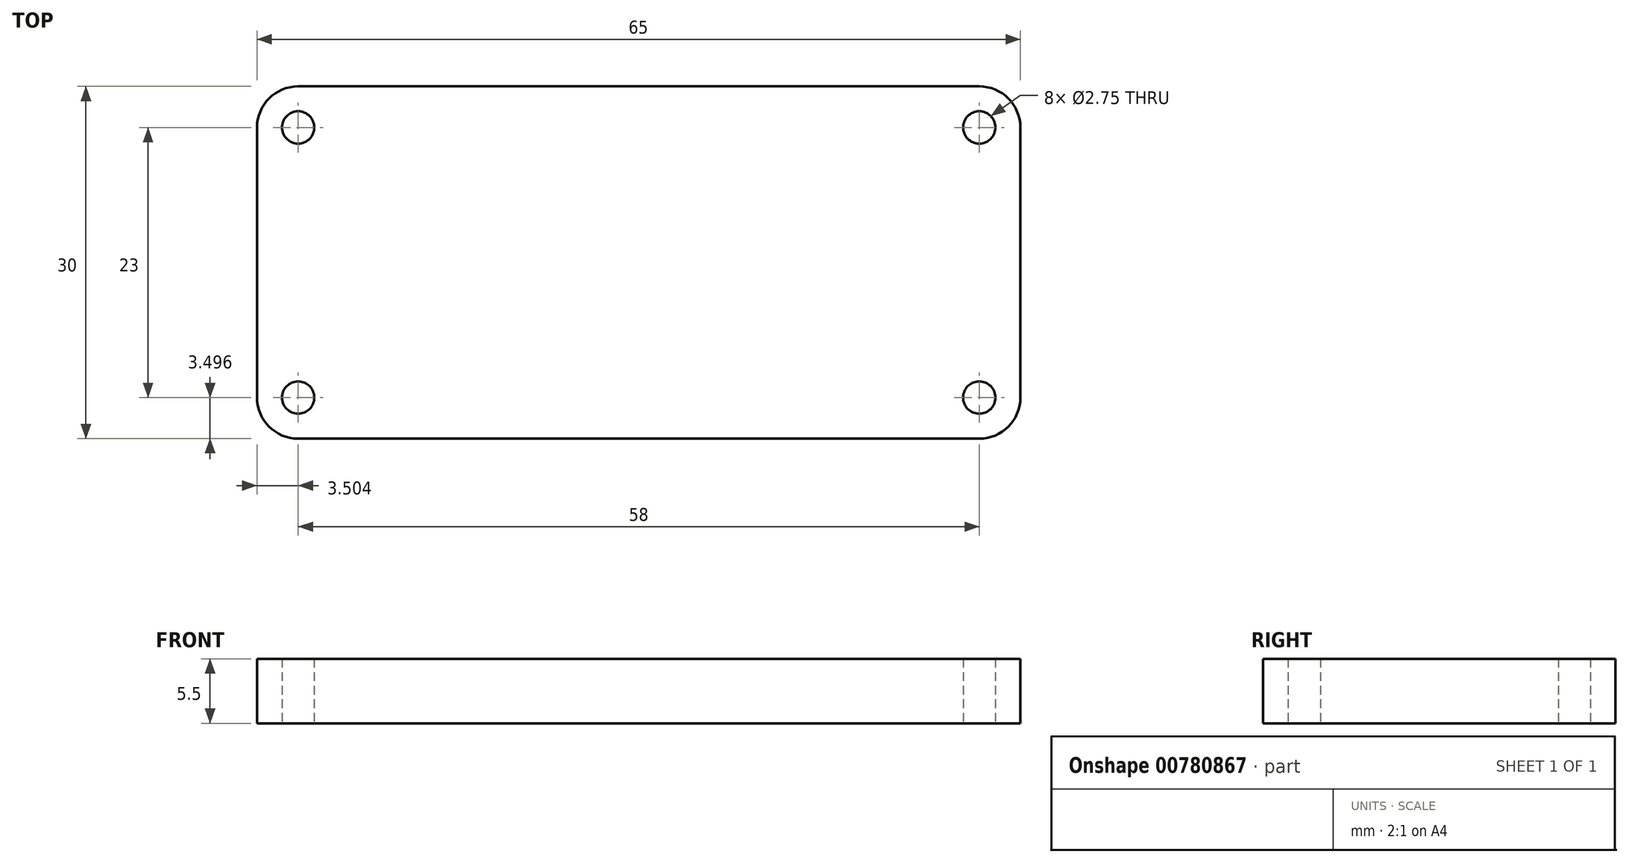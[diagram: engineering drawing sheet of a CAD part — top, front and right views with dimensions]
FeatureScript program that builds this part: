
annotation { "Feature Type Name" : "Feature", "Feature Type Description" : "" }
export const myFeature = defineFeature(function(context is Context, id is Id, definition is map)
    precondition{}
    {
        {
            var Q0;
            Q0=qCreatedBy(makeId("Top.planeOp"),FACE);
            var sketch = newSketch(context, id + "F0", { "sketchPlane" : qUnion([Q0])});
            skLineSegment(sketch, "E0.bottom", {"start": v(-24.73, 20.18) * mm, "end": v(33.27, 20.18) * mm});
            skLineSegment(sketch, "E0.top", {"start": v(-24.73, -9.82) * mm, "end": v(33.27, -9.82) * mm});
            skLineSegment(sketch, "E0.left", {"start": v(-28.23, 16.68) * mm, "end": v(-28.23, -6.32) * mm});
            skLineSegment(sketch, "E0.right", {"start": v(36.77, 16.68) * mm, "end": v(36.77, -6.32) * mm});
            skPoint(sketch, "E1.visualSharp", {"position": v(-28.23, 20.18) * mm});
            skArc(sketch, "E1.filletArc", {"start": v(-24.73, 20.18) * mm, "mid": v(-27.2, 19.15) * mm, "end": v(-28.23, 16.68) * mm});
            skPoint(sketch, "E2.visualSharp", {"position": v(-28.23, -9.82) * mm});
            skArc(sketch, "E2.filletArc", {"start": v(-28.23, -6.32) * mm, "mid": v(-27.2, -8.8) * mm, "end": v(-24.73, -9.82) * mm});
            skPoint(sketch, "E3.visualSharp", {"position": v(36.77, -9.82) * mm});
            skArc(sketch, "E3.filletArc", {"start": v(33.27, -9.82) * mm, "mid": v(35.75, -8.8) * mm, "end": v(36.77, -6.32) * mm});
            skPoint(sketch, "E4.visualSharp", {"position": v(36.77, 20.18) * mm});
            skArc(sketch, "E4.filletArc", {"start": v(36.77, 16.68) * mm, "mid": v(35.75, 19.15) * mm, "end": v(33.27, 20.18) * mm});
            skCircle(sketch, "E5", {"center": v(-24.73, -6.32) * mm, "radius": 1.75 * mm});
            skCircle(sketch, "E6", {"center": v(-24.73, 16.68) * mm, "radius": 1.75 * mm});
            skCircle(sketch, "E7", {"center": v(33.27, 16.68) * mm, "radius": 1.75 * mm});
            skCircle(sketch, "E8", {"center": v(33.27, -6.32) * mm, "radius": 1.75 * mm});
            skPoint(sketch, "E9", {"position": v(4.27, 20.18) * mm});
            skCircle(sketch, "E10", {"center": v(-24.73, -6.32) * mm, "radius": 1.38 * mm});
            skCircle(sketch, "E11", {"center": v(-24.73, 16.68) * mm, "radius": 1.38 * mm});
            skCircle(sketch, "E12", {"center": v(33.27, 16.68) * mm, "radius": 1.38 * mm});
            skCircle(sketch, "E13", {"center": v(33.27, -6.32) * mm, "radius": 1.38 * mm});
            skSolve(sketch);
        }
        {
            var Q0;
            Q0=makeQuery(id+"F0.imprint","IMPRINT",FACE,{"disambiguationData":[TD([[makeQuery(id+"F0.imprint","IMPRINT",EDGE,{"derivedFrom":sQuery(id+"F0.wireOp",EDGE,"E5")}),1.0]])]});
            var Q1;
            Q1=makeQuery(id+"F0.imprint","IMPRINT",FACE,{"disambiguationData":[TD([[makeQuery(id+"F0.imprint","IMPRINT",EDGE,{"derivedFrom":sQuery(id+"F0.wireOp",EDGE,"E6")}),1.0]])]});
            var Q2;
            Q2=makeQuery(id+"F0.imprint","IMPRINT",FACE,{"disambiguationData":[TD([[makeQuery(id+"F0.imprint","IMPRINT",EDGE,{"derivedFrom":sQuery(id+"F0.wireOp",EDGE,"E8")}),1.0]])]});
            var Q3;
            Q3=makeQuery(id+"F0.imprint","IMPRINT",FACE,{"disambiguationData":[TD([[makeQuery(id+"F0.imprint","IMPRINT",EDGE,{"derivedFrom":sQuery(id+"F0.wireOp",EDGE,"E0.bottom")}),-1.0]])]});
            var Q4;
            Q4=makeQuery(id+"F0.imprint","IMPRINT",FACE,{"disambiguationData":[TD([[makeQuery(id+"F0.imprint","IMPRINT",EDGE,{"derivedFrom":sQuery(id+"F0.wireOp",EDGE,"E7")}),1.0]])]});
            var Q5;
            Q5=sQuery(id+"F0.wireOp",EDGE,"E0.top");
            var Q6;
            Q6=sQuery(id+"F0.wireOp",EDGE,"E2.filletArc");
            var Q7;
            Q7=sQuery(id+"F0.wireOp",EDGE,"E0.left");
            var Q8;
            Q8=sQuery(id+"F0.wireOp",EDGE,"E1.filletArc");
            var Q9;
            Q9=sQuery(id+"F0.wireOp",EDGE,"E0.bottom");
            var Q10;
            Q10=sQuery(id+"F0.wireOp",EDGE,"E4.filletArc");
            var Q11;
            Q11=sQuery(id+"F0.wireOp",EDGE,"E0.right");
            var Q12;
            Q12=sQuery(id+"F0.wireOp",EDGE,"E3.filletArc");
            var Q13;
            Q13=sQuery(id+"F0.wireOp",EDGE,"E6");
            var Q14;
            Q14=sQuery(id+"F0.wireOp",EDGE,"E10");
            var Q15;
            Q15=sQuery(id+"F0.wireOp",EDGE,"E7");
            var Q16;
            Q16=sQuery(id+"F0.wireOp",EDGE,"E13");
            extrude(context, id + "F1", {"entities" : qUnion([Q0, Q1, Q2, Q3, Q4]), "surfaceEntities" : qUnion([Q5, Q6, Q7, Q8, Q9, Q10, Q11, Q12, Q13, Q14, Q15, Q16]), "depth" : 5.5 * mm, "offsetDistance" : 25 * mm});
        }
    });
